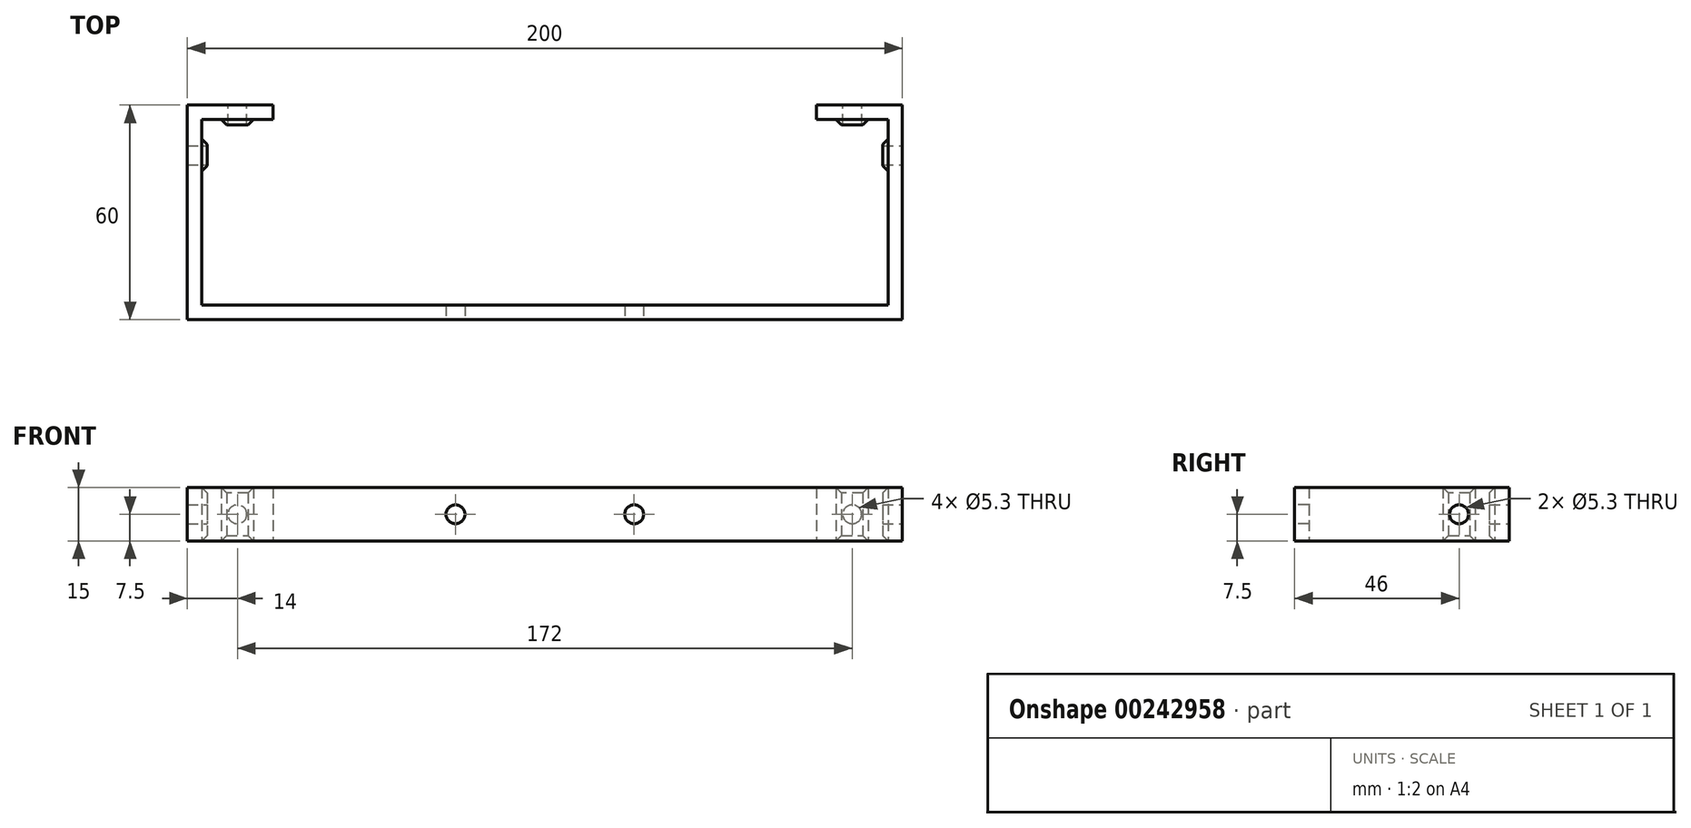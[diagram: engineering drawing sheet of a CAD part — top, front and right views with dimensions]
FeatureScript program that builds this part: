
annotation { "Feature Type Name" : "Feature", "Feature Type Description" : "" }
export const myFeature = defineFeature(function(context is Context, id is Id, definition is map)
    precondition{}
    {
        {
            var Q0;
            Q0=qCreatedBy(makeId("Top.planeOp"),FACE);
            var sketch = newSketch(context, id + "F0", { "sketchPlane" : qUnion([Q0])});
            skLineSegment(sketch, "E0", {"start": v(0, 0) * mm, "end": v(0, 60) * mm});
            skLineSegment(sketch, "E1", {"start": v(4, 4) * mm, "end": v(196, 4) * mm});
            skLineSegment(sketch, "E2", {"start": v(200, 60) * mm, "end": v(200, 0) * mm});
            skLineSegment(sketch, "E3", {"start": v(200, 0) * mm, "end": v(0, 0) * mm});
            skLineSegment(sketch, "E4", {"start": v(0, 60) * mm, "end": v(24, 60) * mm});
            skLineSegment(sketch, "E5", {"start": v(24, 60) * mm, "end": v(24, 56) * mm});
            skLineSegment(sketch, "E6", {"start": v(4, 4) * mm, "end": v(4, 56) * mm});
            skLineSegment(sketch, "E7", {"start": v(4, 56) * mm, "end": v(24, 56) * mm});
            skLineSegment(sketch, "E8", {"start": v(200, 60) * mm, "end": v(176, 60) * mm});
            skLineSegment(sketch, "E9", {"start": v(176, 60) * mm, "end": v(176, 56) * mm});
            skLineSegment(sketch, "E10", {"start": v(176, 56) * mm, "end": v(196, 56) * mm});
            skLineSegment(sketch, "E11", {"start": v(196, 56) * mm, "end": v(196, 4) * mm});
            skSolve(sketch);
        }
        {
            var Q0;
            Q0 = qSketchRegion(id + "F0", true);
            extrude(context, id + "F1", {"entities" : qUnion([Q0]), "depth" : 15 * mm});
        }
        {
            var Q0;
            Q0=qCreatedBy(makeId("Top.planeOp"),FACE);
            var sketch = newSketch(context, id + "F2", { "sketchPlane" : qUnion([Q0])});
            skLineSegment(sketch, "E12.0.0", {"start": v(196, 4) * mm, "end": v(4, 4) * mm, "construction": true});
            skLineSegment(sketch, "E12.0.1", {"start": v(4, 4) * mm, "end": v(4, 56) * mm, "construction": true});
            skLineSegment(sketch, "E12.0.2", {"start": v(4, 56) * mm, "end": v(24, 56) * mm, "construction": true});
            skLineSegment(sketch, "E12.0.3", {"start": v(24, 56) * mm, "end": v(24, 60) * mm, "construction": true});
            skLineSegment(sketch, "E12.0.4", {"start": v(24, 60) * mm, "end": v(0, 60) * mm, "construction": true});
            skLineSegment(sketch, "E12.0.5", {"start": v(0, 60) * mm, "end": v(0, 0) * mm, "construction": true});
            skLineSegment(sketch, "E12.0.6", {"start": v(0, 0) * mm, "end": v(200, 0) * mm, "construction": true});
            skLineSegment(sketch, "E12.0.7", {"start": v(200, 0) * mm, "end": v(200, 60) * mm, "construction": true});
            skLineSegment(sketch, "E12.0.8", {"start": v(200, 60) * mm, "end": v(176, 60) * mm, "construction": true});
            skLineSegment(sketch, "E12.0.9", {"start": v(176, 60) * mm, "end": v(176, 56) * mm, "construction": true});
            skLineSegment(sketch, "E12.0.10", {"start": v(176, 56) * mm, "end": v(196, 56) * mm, "construction": true});
            skLineSegment(sketch, "E12.0.11", {"start": v(196, 56) * mm, "end": v(196, 4) * mm, "construction": true});
            skLineSegment(sketch, "E13", {"start": v(18.5, 56) * mm, "end": v(9.5, 56) * mm});
            skLineSegment(sketch, "E14", {"start": v(9.5, 56) * mm, "end": v(11, 54.5) * mm});
            skLineSegment(sketch, "E15", {"start": v(11, 54.5) * mm, "end": v(17, 54.5) * mm});
            skLineSegment(sketch, "E16", {"start": v(17, 54.5) * mm, "end": v(18.5, 56) * mm});
            skLineSegment(sketch, "E17", {"start": v(4, 50.5) * mm, "end": v(4, 41.5) * mm});
            skLineSegment(sketch, "E18", {"start": v(4, 41.5) * mm, "end": v(5.5, 43) * mm});
            skLineSegment(sketch, "E19", {"start": v(5.5, 43) * mm, "end": v(5.5, 49) * mm});
            skLineSegment(sketch, "E20", {"start": v(5.5, 49) * mm, "end": v(4, 50.5) * mm});
            skLineSegment(sketch, "E21", {"start": v(100, 4) * mm, "end": v(100, 81.88) * mm, "construction": true});
            skLineSegment(sketch, "E22.MirrorCS", {"start": v(196, 50.5) * mm, "end": v(196, 41.5) * mm});
            skLineSegment(sketch, "E23.MirrorCS", {"start": v(196, 41.5) * mm, "end": v(194.5, 43) * mm});
            skLineSegment(sketch, "E24.MirrorCS", {"start": v(194.5, 43) * mm, "end": v(194.5, 49) * mm});
            skLineSegment(sketch, "E25.MirrorCS", {"start": v(194.5, 49) * mm, "end": v(196, 50.5) * mm});
            skLineSegment(sketch, "E26.MirrorCS", {"start": v(190.5, 56) * mm, "end": v(189, 54.5) * mm});
            skLineSegment(sketch, "E27.MirrorCS", {"start": v(183, 54.5) * mm, "end": v(181.5, 56) * mm});
            skLineSegment(sketch, "E28.MirrorCS", {"start": v(189, 54.5) * mm, "end": v(183, 54.5) * mm});
            skLineSegment(sketch, "E29.MirrorCS", {"start": v(181.5, 56) * mm, "end": v(190.5, 56) * mm});
            skSolve(sketch);
        }
        {
            var Q0;
            Q0 = qSketchRegion(id + "F2", true);
            var Q1;
            Q1=makeQuery(id+"F1.opExtrude","CAP_FACE",FACE,{"disambiguationData":[OSD([sQuery(id+"F0.wireOp",EDGE,"E0"),sQuery(id+"F0.wireOp",EDGE,"E1"),sQuery(id+"F0.wireOp",EDGE,"E2"),sQuery(id+"F0.wireOp",EDGE,"E3"),sQuery(id+"F0.wireOp",EDGE,"E4"),sQuery(id+"F0.wireOp",EDGE,"E5"),sQuery(id+"F0.wireOp",EDGE,"E6"),sQuery(id+"F0.wireOp",EDGE,"E7"),sQuery(id+"F0.wireOp",EDGE,"E8"),sQuery(id+"F0.wireOp",EDGE,"E9"),sQuery(id+"F0.wireOp",EDGE,"E10"),sQuery(id+"F0.wireOp",EDGE,"E11")])],"isStart":false});
            extrude(context, id + "F3", {"entities" : qUnion([Q0]), "operationType" : NewBodyOperationType.ADD, "endBound" : BoundingType.UP_TO_SURFACE, "endBoundEntityFace" : qUnion([Q1]), "depth" : 25 * mm});
        }
        {
            var Q0;
            Q0=makeQuery(id+"F3.opExtrude","CAP_EDGE",EDGE,{"disambiguationData":[OSD([sQuery(id+"F2.wireOp",EDGE,"E19")])],"isStart":false});
            var Q1;
            Q1=makeQuery(id+"F3.opExtrude","CAP_EDGE",EDGE,{"disambiguationData":[OSD([sQuery(id+"F2.wireOp",EDGE,"E19")])],"isStart":true});
            var Q2;
            Q2=makeQuery(id+"F3.opExtrude","CAP_EDGE",EDGE,{"disambiguationData":[OSD([sQuery(id+"F2.wireOp",EDGE,"E15")])],"isStart":true});
            var Q3;
            Q3=makeQuery(id+"F3.opExtrude","CAP_EDGE",EDGE,{"disambiguationData":[OSD([sQuery(id+"F2.wireOp",EDGE,"E15")])],"isStart":false});
            var Q4;
            Q4=makeQuery(id+"F3.opExtrude","CAP_EDGE",EDGE,{"disambiguationData":[OSD([sQuery(id+"F2.wireOp",EDGE,"E28.MirrorCS")])],"isStart":false});
            var Q5;
            Q5=makeQuery(id+"F3.opExtrude","CAP_EDGE",EDGE,{"disambiguationData":[OSD([sQuery(id+"F2.wireOp",EDGE,"E24.MirrorCS")])],"isStart":false});
            var Q6;
            Q6=makeQuery(id+"F3.opExtrude","CAP_EDGE",EDGE,{"disambiguationData":[OSD([sQuery(id+"F2.wireOp",EDGE,"E24.MirrorCS")])],"isStart":true});
            var Q7;
            Q7=makeQuery(id+"F3.opExtrude","CAP_EDGE",EDGE,{"disambiguationData":[OSD([sQuery(id+"F2.wireOp",EDGE,"E28.MirrorCS")])],"isStart":true});
            chamfer(context, id + "F4", {"entities" : qUnion([Q0, Q1, Q2, Q3, Q4, Q5, Q6, Q7]), "width" : 1.5 * mm, "tangentPropagation" : true});
        }
        {
            var Q0;
            Q0=makeQuery(id+"F1.opExtrude","SWEPT_FACE",FACE,{"disambiguationData":[OSD([sQuery(id+"F0.wireOp",EDGE,"E3")])]});
            var sketch = newSketch(context, id + "F5", { "sketchPlane" : qUnion([Q0])});
            skCircle(sketch, "E30", {"center": v(75, 7.5) * mm, "radius": 2.65 * mm});
            skCircle(sketch, "E31", {"center": v(125, 7.5) * mm, "radius": 2.65 * mm});
            skSolve(sketch);
        }
        {
            var Q0;
            Q0 = qSketchRegion(id + "F5", true);
            extrude(context, id + "F6", {"entities" : qUnion([Q0]), "operationType" : NewBodyOperationType.REMOVE, "endBound" : BoundingType.UP_TO_NEXT, "oppositeDirection" : true, "depth" : 25 * mm});
        }
        {
            var Q0;
            Q0=makeQuery(id+"F1.opExtrude","SWEPT_FACE",FACE,{"disambiguationData":[OSD([sQuery(id+"F0.wireOp",EDGE,"E2")])]});
            var sketch = newSketch(context, id + "F7", { "sketchPlane" : qUnion([Q0])});
            skLineSegment(sketch, "E32.0.0", {"start": v(49, 13.5) * mm, "end": v(49, 1.5) * mm, "construction": true});
            skLineSegment(sketch, "E32.0.1", {"start": v(49, 1.5) * mm, "end": v(43, 1.5) * mm, "construction": true});
            skLineSegment(sketch, "E32.0.2", {"start": v(43, 1.5) * mm, "end": v(43, 13.5) * mm, "construction": true});
            skLineSegment(sketch, "E32.0.3", {"start": v(43, 13.5) * mm, "end": v(49, 13.5) * mm, "construction": true});
            skCircle(sketch, "E33", {"center": v(46, 7.5) * mm, "radius": 2.65 * mm});
            skPoint(sketch, "E33.centerSnap0", {"position": v(49, 7.5) * mm});
            skPoint(sketch, "E33.centerSnap1", {"position": v(46, 13.5) * mm});
            skSolve(sketch);
        }
        {
            var Q0;
            Q0 = qSketchRegion(id + "F7", true);
            extrude(context, id + "F8", {"entities" : qUnion([Q0]), "operationType" : NewBodyOperationType.REMOVE, "endBound" : BoundingType.THROUGH_ALL, "oppositeDirection" : true, "depth" : 25 * mm});
        }
        {
            var Q0;
            Q0=makeQuery(id+"F1.opExtrude","SWEPT_FACE",FACE,{"disambiguationData":[OSD([sQuery(id+"F0.wireOp",EDGE,"E8")])]});
            var sketch = newSketch(context, id + "F9", { "sketchPlane" : qUnion([Q0])});
            skLineSegment(sketch, "E34.0.0", {"start": v(-183, 13.5) * mm, "end": v(-183, 1.5) * mm, "construction": true});
            skLineSegment(sketch, "E34.0.1", {"start": v(-183, 1.5) * mm, "end": v(-189, 1.5) * mm, "construction": true});
            skLineSegment(sketch, "E34.0.2", {"start": v(-189, 1.5) * mm, "end": v(-189, 13.5) * mm, "construction": true});
            skLineSegment(sketch, "E34.0.3", {"start": v(-189, 13.5) * mm, "end": v(-183, 13.5) * mm, "construction": true});
            skLineSegment(sketch, "E35.0.0", {"start": v(-17, 1.5) * mm, "end": v(-17, 13.5) * mm, "construction": true});
            skLineSegment(sketch, "E35.0.1", {"start": v(-17, 13.5) * mm, "end": v(-11, 13.5) * mm, "construction": true});
            skLineSegment(sketch, "E35.0.2", {"start": v(-11, 13.5) * mm, "end": v(-11, 1.5) * mm, "construction": true});
            skLineSegment(sketch, "E35.0.3", {"start": v(-11, 1.5) * mm, "end": v(-17, 1.5) * mm, "construction": true});
            skCircle(sketch, "E36", {"center": v(-186, 7.5) * mm, "radius": 2.65 * mm});
            skPoint(sketch, "E36.centerSnap0", {"position": v(-183, 7.5) * mm});
            skPoint(sketch, "E36.centerSnap1", {"position": v(-186, 13.5) * mm});
            skLineSegment(sketch, "E37.0.0", {"start": v(-196, 0) * mm, "end": v(-4, 0) * mm, "construction": true});
            skLineSegment(sketch, "E37.0.1", {"start": v(-4, 0) * mm, "end": v(-4, 15) * mm, "construction": true});
            skLineSegment(sketch, "E37.0.2", {"start": v(-4, 15) * mm, "end": v(-196, 15) * mm, "construction": true});
            skLineSegment(sketch, "E37.0.3", {"start": v(-196, 15) * mm, "end": v(-196, 0) * mm, "construction": true});
            skLineSegment(sketch, "E38", {"start": v(-100, 15) * mm, "end": v(-100, 0) * mm, "construction": true});
            skCircle(sketch, "E39.MirrorC", {"center": v(-14, 7.5) * mm, "radius": 2.65 * mm});
            skSolve(sketch);
        }
        {
            var Q0;
            Q0 = qSketchRegion(id + "F9", true);
            extrude(context, id + "F10", {"entities" : qUnion([Q0]), "operationType" : NewBodyOperationType.REMOVE, "endBound" : BoundingType.UP_TO_NEXT, "oppositeDirection" : true, "depth" : 25 * mm});
        }
    });
